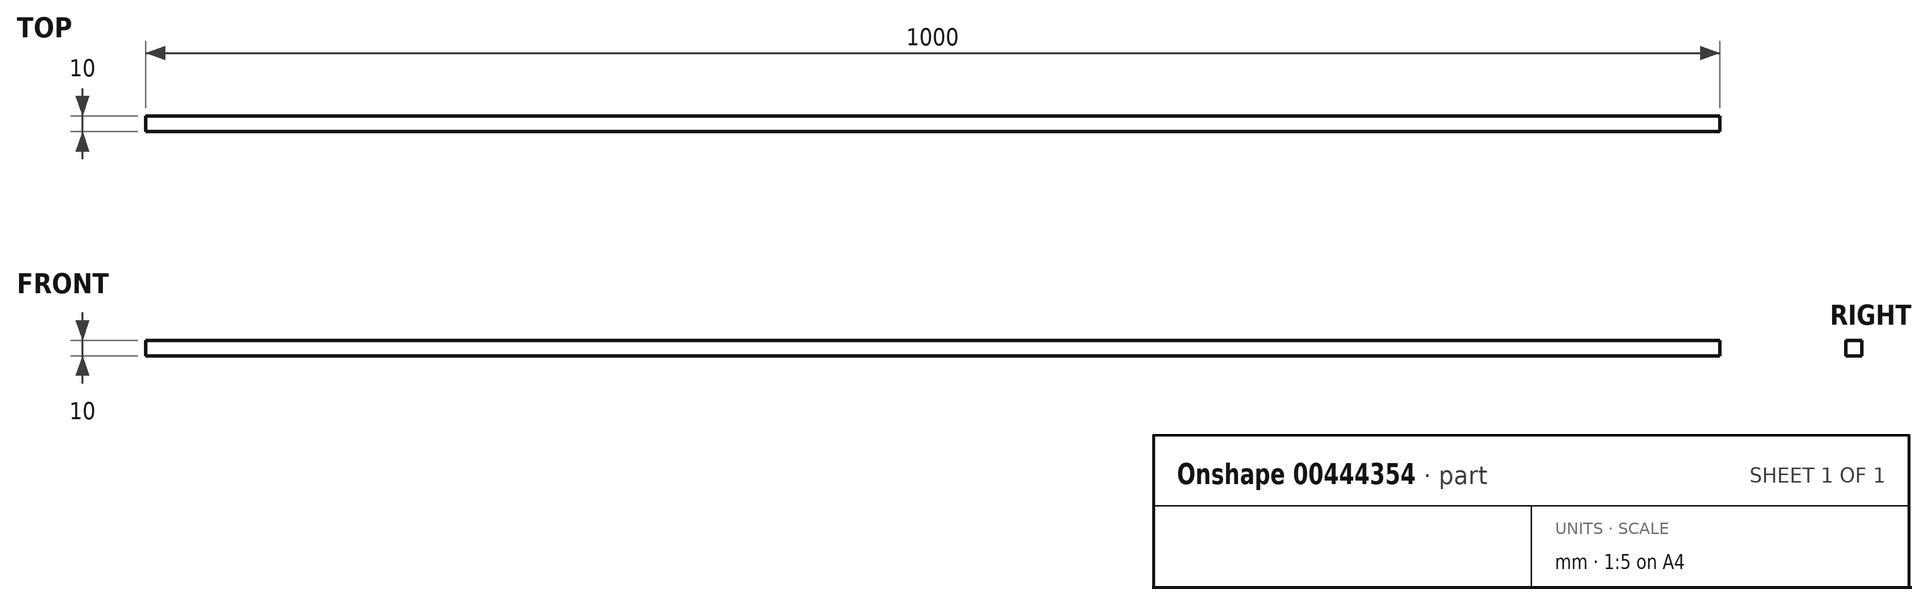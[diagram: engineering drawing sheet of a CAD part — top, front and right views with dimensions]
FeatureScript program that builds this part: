
annotation { "Feature Type Name" : "Feature", "Feature Type Description" : "" }
export const myFeature = defineFeature(function(context is Context, id is Id, definition is map)
    precondition{}
    {
        {
            var Q0;
            Q0=qCreatedBy(makeId("Right.planeOp"),FACE);
            var sketch = newSketch(context, id + "F0", { "sketchPlane" : qUnion([Q0])});
            skLineSegment(sketch, "E0.bottom", {"start": v(-1.38, 5.05) * mm, "end": v(8.62, 5.05) * mm});
            skLineSegment(sketch, "E0.top", {"start": v(-1.38, -4.95) * mm, "end": v(8.62, -4.95) * mm});
            skLineSegment(sketch, "E0.left", {"start": v(-1.38, 5.05) * mm, "end": v(-1.38, -4.95) * mm});
            skLineSegment(sketch, "E0.right", {"start": v(8.62, 5.05) * mm, "end": v(8.62, -4.95) * mm});
            skSolve(sketch);
        }
        {
            var Q0;
            Q0=makeQuery(id+"F0.imprint","IMPRINT",FACE,{"disambiguationData":[TD([[makeQuery(id+"F0.imprint","IMPRINT",EDGE,{"derivedFrom":sQuery(id+"F0.wireOp",EDGE,"E0.bottom")}),-1.0]])]});
            var Q1;
            Q1 = qSketchRegion(id + "F0", true);
            extrude(context, id + "F1", {"entities" : qUnion([Q0, Q1]), "depth" : 1000 * mm});
        }
    });
